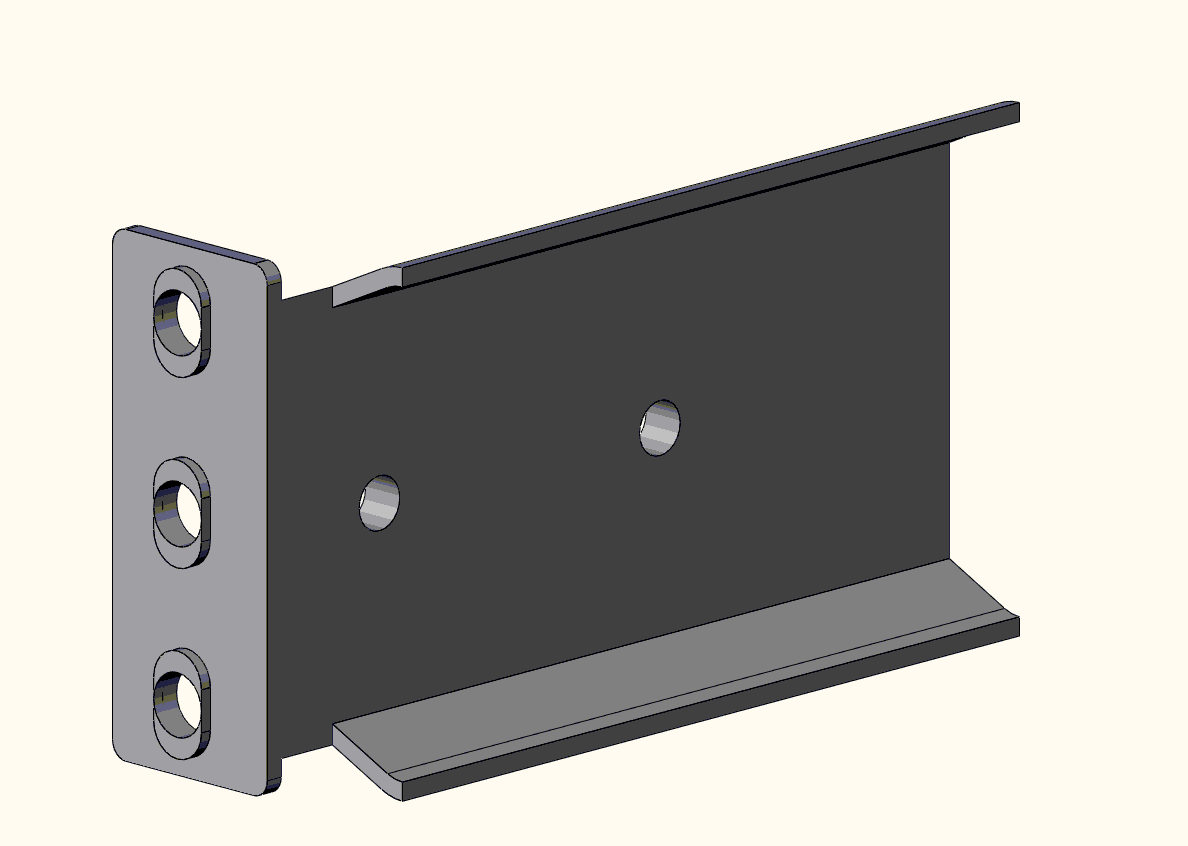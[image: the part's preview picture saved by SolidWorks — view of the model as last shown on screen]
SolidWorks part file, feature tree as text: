
SOLIDWORKS PART (.sldprt)
format: sldprt  version: not decoded by parser v0  size: 257,024 bytes
history: native  units: mm
features: sketch x6, extrude x4, pattern_linear x2, cut_extrude x2, material x1, plane x1 (+11 scaffold rows collapsed)
feature tree (27):
  scaffold x11  (default folders/planes/origin — collapsed)
  material  "Material <not specified>"
  plane  "Side"
  sketch  "Sketch1"  dims[c1.D3=7.9375mm c1.D4=11.1125mm c1.D1=1.5875mm c1.D2=9.525mm c1.D5=~7.661346mm c2.D5=65.0deg c2.D6=20.574mm c2.D7=20.574mm c2.D8=~40.609749mm c3.D8=65.0deg]
  extrude  "Base-Extrude"  Depth=77.216mm
  sketch  "Sketch2"  dims[c1.D7=3.7mm c1.D8=1.524mm c1.D9=1.524mm c1.D10=1.524mm c2.D7=5.4102mm c2.D11=5.4102mm c2.D2=44.196mm c2.D3=15.875mm c2.D4=15.875mm c2.D5=1.524mm c2.D6=13.97mm c3.D11=9.144mm c3.D1=17.526mm]
  extrude  "Boss-Extrude1"  [1 undecoded]
  sketch  "Sketch8"  dims[D1=8.9916mm D2=~5.41274mm]
  extrude  "Extrude1"  Depth=1.016mm
  pattern_linear  "LPattern1"  Count1=3 Count2=1 Spacing1=15.875mm Spacing2=50mm
  sketch  "Sketch3"  dims[D1=5.08mm D2=7.366mm D3=2.286mm D4=2.286mm]
  cut_extrude  "Cut-Extrude1"  [1 undecoded]
  sketch  "Sketch7"  dims[c1.D5=4.6mm c1.D2=4.6mm c1.D1=12.7mm c2.D2=28.702mm c2.D3=4.826mm c2.D4=63.5mm c3.D2=31.75mm]
  cut_extrude  "Cut-Extrude3"  [1 undecoded]
  sketch  "Sketch9"  dims[D1=7.239mm]
  extrude  "Extrude2"  Depth=2.286mm
  pattern_linear  "LPattern2"  Count1=2 Count2=1 Spacing1=31.75mm Spacing2=50mm
decode coverage: 11 of 14 modeling features carry decoded parameters
note: ~ marks probable driven/reference dimensions
note: 3 parameter values undecoded
summary: no parameter record found for 3 features
note: suppression state not decoded; provenance and decode notes live in map.json
